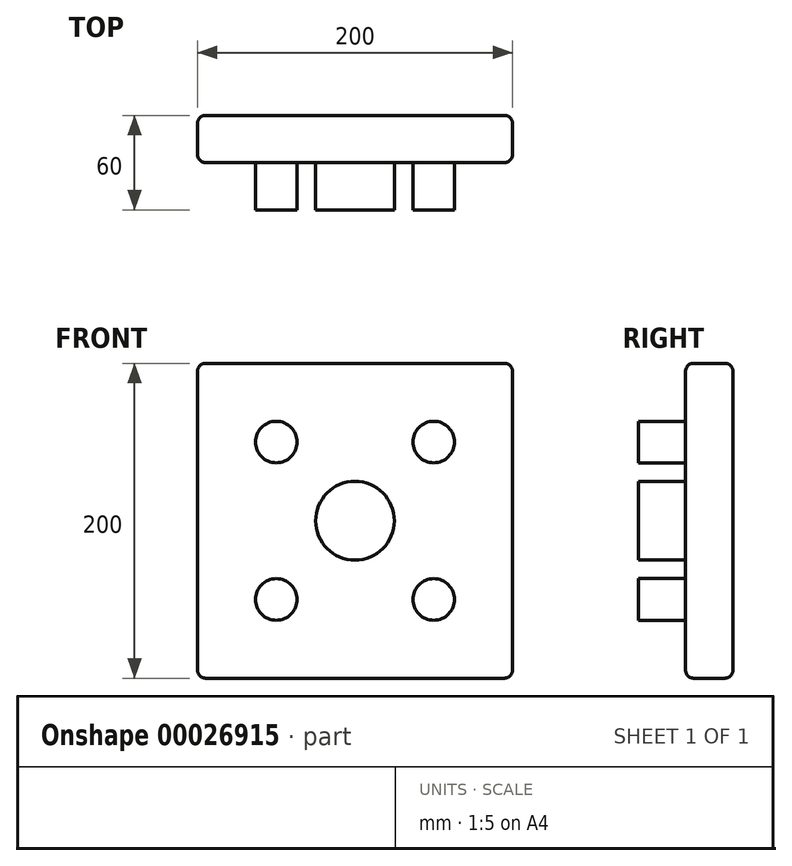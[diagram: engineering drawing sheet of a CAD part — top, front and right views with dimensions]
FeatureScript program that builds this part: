
annotation { "Feature Type Name" : "Feature", "Feature Type Description" : "" }
export const myFeature = defineFeature(function(context is Context, id is Id, definition is map)
    precondition{}
    {
        {
            var Q0;
            Q0=qCreatedBy(makeId("Front.planeOp"),FACE);
            var sketch = newSketch(context, id + "F0", { "sketchPlane" : qUnion([Q0])});
            skLineSegment(sketch, "E0.bottom", {"start": v(-100, 100) * mm, "end": v(100, 100) * mm});
            skLineSegment(sketch, "E0.top", {"start": v(-100, -100) * mm, "end": v(100, -100) * mm});
            skLineSegment(sketch, "E0.left", {"start": v(-100, 100) * mm, "end": v(-100, -100) * mm});
            skLineSegment(sketch, "E0.right", {"start": v(100, 100) * mm, "end": v(100, -100) * mm});
            skSolve(sketch);
        }
        {
            var Q0;
            Q0 = qSketchRegion(id + "F0", true);
            extrude(context, id + "F1", {"entities" : qUnion([Q0]), "depth" : 30 * mm});
        }
        {
            var Q0;
            Q0=makeQuery(id+"F1.opExtrude","CAP_FACE",FACE,{"disambiguationData":[OSD([sQuery(id+"F0.wireOp",EDGE,"E0.bottom"),sQuery(id+"F0.wireOp",EDGE,"E0.top"),sQuery(id+"F0.wireOp",EDGE,"E0.left"),sQuery(id+"F0.wireOp",EDGE,"E0.right")])],"isStart":false});
            var sketch = newSketch(context, id + "F2", { "sketchPlane" : qUnion([Q0])});
            skCircle(sketch, "E1", {"center": v(0, 0) * mm, "radius": 25 * mm});
            skSolve(sketch);
        }
        {
            var Q0;
            Q0=makeQuery(id+"F2.imprint","IMPRINT",FACE,{"disambiguationData":[TD([[makeQuery(id+"F2.imprint","IMPRINT",EDGE,{"derivedFrom":sQuery(id+"F2.wireOp",EDGE,"E1")}),1.0]])]});
            extrude(context, id + "F3", {"entities" : qUnion([Q0]), "operationType" : NewBodyOperationType.ADD, "depth" : 30 * mm});
        }
        {
            var Q0;
            Q0=makeQuery(id+"F1.opExtrude","CAP_FACE",FACE,{"disambiguationData":[OSD([sQuery(id+"F0.wireOp",EDGE,"E0.bottom"),sQuery(id+"F0.wireOp",EDGE,"E0.top"),sQuery(id+"F0.wireOp",EDGE,"E0.left"),sQuery(id+"F0.wireOp",EDGE,"E0.right")])],"isStart":false});
            var sketch = newSketch(context, id + "F4", { "sketchPlane" : qUnion([Q0])});
            skCircle(sketch, "E2", {"center": v(-50, -50) * mm, "radius": 13.2 * mm});
            skCircle(sketch, "E3.0.1.0", {"center": v(-50, 50) * mm, "radius": 13.2 * mm});
            skCircle(sketch, "E3.1.0.0", {"center": v(50, -50) * mm, "radius": 13.2 * mm});
            skCircle(sketch, "E3.1.1.0", {"center": v(50, 50) * mm, "radius": 13.2 * mm});
            skLineSegment(sketch, "E3.direction1", {"start": v(-50, -50) * mm, "end": v(50, -50) * mm, "construction": true});
            skLineSegment(sketch, "E3.direction2", {"start": v(-50, -50) * mm, "end": v(-50, 50) * mm, "construction": true});
            skLineSegment(sketch, "E4", {"start": v(-66.92, 0) * mm, "end": v(60.8, 0) * mm});
            skLineSegment(sketch, "E5", {"start": v(0, -49.75) * mm, "end": v(0, 68.34) * mm});
            skSolve(sketch);
        }
        {
            var Q0;
            Q0=makeQuery(id+"F4.imprint","IMPRINT",FACE,{"disambiguationData":[TD([[makeQuery(id+"F4.imprint","IMPRINT",EDGE,{"derivedFrom":sQuery(id+"F4.wireOp",EDGE,"E3.0.1.0")}),1.0]])]});
            var Q1;
            Q1=makeQuery(id+"F4.imprint","IMPRINT",FACE,{"disambiguationData":[TD([[makeQuery(id+"F4.imprint","IMPRINT",EDGE,{"derivedFrom":sQuery(id+"F4.wireOp",EDGE,"E3.1.1.0")}),1.0]])]});
            var Q2;
            Q2=makeQuery(id+"F4.imprint","IMPRINT",FACE,{"disambiguationData":[TD([[makeQuery(id+"F4.imprint","IMPRINT",EDGE,{"derivedFrom":sQuery(id+"F4.wireOp",EDGE,"E3.1.0.0")}),1.0]])]});
            var Q3;
            Q3=makeQuery(id+"F4.imprint","IMPRINT",FACE,{"disambiguationData":[TD([[makeQuery(id+"F4.imprint","IMPRINT",EDGE,{"derivedFrom":sQuery(id+"F4.wireOp",EDGE,"E2")}),1.0]])]});
            extrude(context, id + "F5", {"entities" : qUnion([Q0, Q1, Q2, Q3]), "operationType" : NewBodyOperationType.ADD, "depth" : 30 * mm});
        }
        {
            var Q0;
            Q0=makeQuery(id+"F1.opExtrude","SWEPT_FACE",FACE,{"disambiguationData":[OSD([sQuery(id+"F0.wireOp",EDGE,"E0.right")])]});
            var Q1;
            Q1=makeQuery(id+"F1.opExtrude","SWEPT_FACE",FACE,{"disambiguationData":[OSD([sQuery(id+"F0.wireOp",EDGE,"E0.top")])]});
            var Q2;
            Q2=makeQuery(id+"F1.opExtrude","CAP_EDGE",EDGE,{"disambiguationData":[OSD([sQuery(id+"F0.wireOp",EDGE,"E0.top")])],"isStart":true});
            var Q3;
            Q3=makeQuery(id+"F1.opExtrude","SWEPT_FACE",FACE,{"disambiguationData":[OSD([sQuery(id+"F0.wireOp",EDGE,"E0.left")])]});
            var Q4;
            Q4=makeQuery(id+"F1.opExtrude","SWEPT_FACE",FACE,{"disambiguationData":[OSD([sQuery(id+"F0.wireOp",EDGE,"E0.bottom")])]});
            fillet(context, id + "F6", {"entities" : qUnion([Q0, Q1, Q2, Q3, Q4]), "radius" : 5 * mm, "tangentPropagation" : true, "allowEdgeOverflow" : false});
        }
    });
